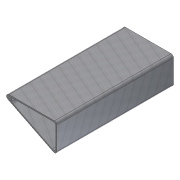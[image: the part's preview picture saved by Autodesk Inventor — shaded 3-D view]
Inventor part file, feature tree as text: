
AUTODESK INVENTOR PART (.ipt)
format: ipt  version: 2012 (Build 160160000, 160)  size: 102,400 bytes
history: native  units: in
note: dims shown in document units (in); Inventor stores cm internally (conversion verified against a paired STEP export)
features: extrude x1, sketch x1
ambient origin geometry x8: Origin, YZ Plane, XZ Plane, XY Plane, X Axis, Y Axis, Z Axis, Center Point
bodies: Solid1 (feature_tree)
feature tree (2):
  extrude  "Extrusion1"  Depth=0.0625in
  sketch  "Sketch1"  dims[d0=0.0625in d1=0.0625in d2=0.0625in d3=3.0in d4=1.5in d5=6.0in d6=0.0in d7=0.125in d8=0.125in]
